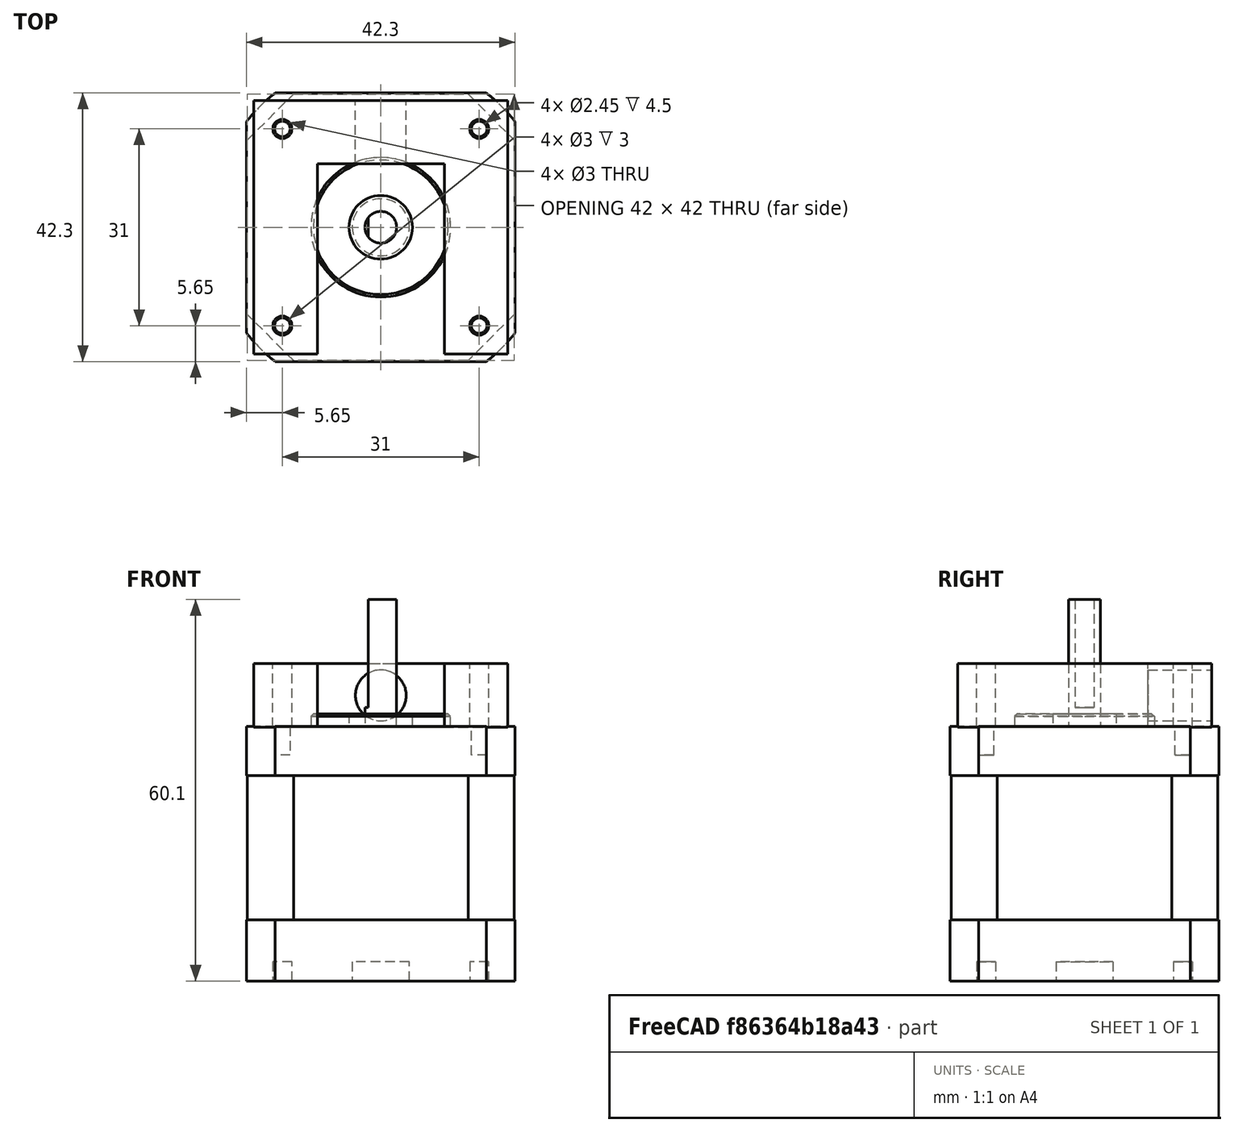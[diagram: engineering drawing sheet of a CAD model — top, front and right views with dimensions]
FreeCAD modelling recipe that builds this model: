
FCSTD DOCUMENT  (FreeCAD 0.17R13522 (Git))
Label: pivot-fastener-nema-17
License: All rights reserved
LicenseURL: http://en.wikipedia.org/wiki/All_rights_reserved
objects: Part::Cylinder×5, Part::Box×2, Part::FeaturePython×1, Part::MultiFuse×1, Part::Cut×1
note: 10 computed .brp shape members not serialized (recipe doc carries the construction recipe); baked Part::Feature solids carry a one-line shape summary decoded from their .brp

FEATURE [Part::Box] Box  label="Cube"
  AttacherType = Attacher::AttachEngine3D
  Height = 10
  Length = 40
  Placement = pos=(-20,-20,-5) rot=(0,0,1;0rad)
  Width = 40
FEATURE [Part::FeaturePython] NEMA_17_Stepper_Motor_40mm_01  # a2plus imported part (geometry in sourceFile) (typed FeaturePython)
  Placement = pos=(0,0,-45) rot=(-1,0,0;0rad)
  fixedPosition = false
  sourceFile = <userpath>/.FreeCAD/Mod/parts_library/Electrical Parts/Motors/NEMA-17_Stepper_Motor_40mm.fcstd
  timeLastImport = 1.5364e+09
  updateColors = true
FEATURE [Part::Box] Box001  label="Cube001"
  AttacherType = Attacher::AttachEngine3D
  Height = 10
  Length = 20
  Placement = pos=(-10,-20,-5) rot=(0,0,1;0rad)
  Width = 30
FEATURE [Part::Cylinder] Cylinder
  Angle = 360
  AttacherType = Attacher::AttachEngine3D
  Height = 10
  Placement = pos=(-15.5,15.5,-5) rot=(0,0,1;0rad)
  Radius = 1.5
FEATURE [Part::Cylinder] Cylinder001
  Angle = 360
  AttacherType = Attacher::AttachEngine3D
  Height = 10
  Placement = pos=(15.5,-15.5,-5) rot=(0,0,1;0rad)
  Radius = 1.5
FEATURE [Part::Cylinder] Cylinder002
  Angle = 360
  AttacherType = Attacher::AttachEngine3D
  Height = 10
  Placement = pos=(-15.5,-15.5,-5) rot=(0,0,1;0rad)
  Radius = 1.5
FEATURE [Part::Cylinder] Cylinder003
  Angle = 360
  AttacherType = Attacher::AttachEngine3D
  Height = 10
  Placement = pos=(15.5,15.5,-5) rot=(0,0,1;0rad)
  Radius = 1.5
FEATURE [Part::Cylinder] Cylinder004
  Angle = 360
  AttacherType = Attacher::AttachEngine3D
  Height = 10
  Placement = pos=(0,10,0) rot=(-1,0,0;1.5708rad)
  Radius = 4
FEATURE [Part::MultiFuse] Fusion
  Shapes = -> [Box001,Cylinder,Cylinder001,Cylinder002,Cylinder003,Cylinder004]
FEATURE [Part::Cut] Cut
  Base = -> Box
  Tool = -> Fusion
